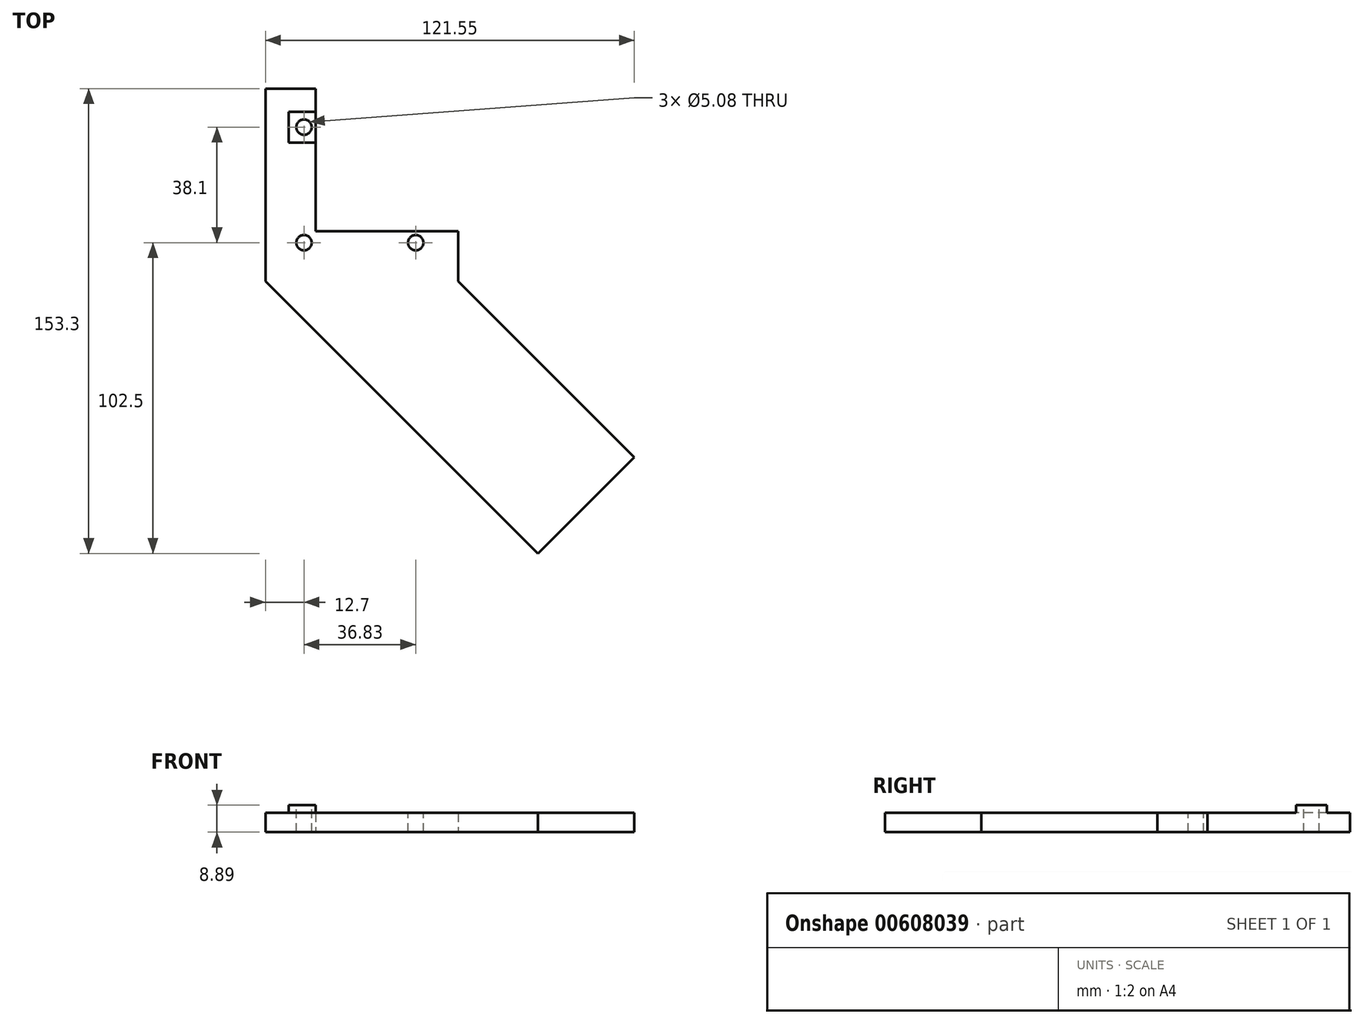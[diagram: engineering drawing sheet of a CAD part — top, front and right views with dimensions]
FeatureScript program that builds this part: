
annotation { "Feature Type Name" : "Feature", "Feature Type Description" : "" }
export const myFeature = defineFeature(function(context is Context, id is Id, definition is map)
    precondition{}
    {
        {
            var Q0;
            Q0=qCreatedBy(makeId("Top.planeOp"),FACE);
            var sketch = newSketch(context, id + "F0", { "sketchPlane" : qUnion([Q0])});
            skLineSegment(sketch, "E0", {"start": v(0, 0) * mm, "end": v(0, 63.5) * mm});
            skLineSegment(sketch, "E1", {"start": v(0, 63.5) * mm, "end": v(16.51, 63.5) * mm});
            skLineSegment(sketch, "E2", {"start": v(16.51, 63.5) * mm, "end": v(16.51, 16.5) * mm});
            skLineSegment(sketch, "E3", {"start": v(16.51, 16.5) * mm, "end": v(63.5, 16.51) * mm});
            skLineSegment(sketch, "E4", {"start": v(63.5, 16.51) * mm, "end": v(63.5, 0) * mm});
            skLineSegment(sketch, "E5", {"start": v(63.5, 0) * mm, "end": v(121.55, -58.05) * mm});
            skLineSegment(sketch, "E6", {"start": v(89.8, -89.8) * mm, "end": v(0, 0) * mm});
            skLineSegment(sketch, "E7", {"start": v(89.8, -89.8) * mm, "end": v(121.55, -58.05) * mm});
            skSolve(sketch);
        }
        {
            var Q0;
            Q0 = qSketchRegion(id + "F0", true);
            extrude(context, id + "F1", {"entities" : qUnion([Q0]), "depth" : 6.35 * mm, "offsetDistance" : 25.4 * mm});
        }
        {
            var Q0;
            Q0=makeQuery(id+"F1.opExtrude","CAP_FACE",FACE,{"disambiguationData":[OSD([sQuery(id+"F0.wireOp",EDGE,"E0"),sQuery(id+"F0.wireOp",EDGE,"E1"),sQuery(id+"F0.wireOp",EDGE,"E2"),sQuery(id+"F0.wireOp",EDGE,"E3"),sQuery(id+"F0.wireOp",EDGE,"E4"),sQuery(id+"F0.wireOp",EDGE,"E5"),sQuery(id+"F0.wireOp",EDGE,"BQdoBjQO-dgXR-ntd8-ExkX-L0m3NcibP9LL"),sQuery(id+"F0.wireOp",EDGE,"E6")])],"isStart":false});
            var sketch = newSketch(context, id + "F2", { "sketchPlane" : qUnion([Q0])});
            skCircle(sketch, "E8", {"center": v(12.7, 50.8) * mm, "radius": 2.54 * mm});
            skCircle(sketch, "E9", {"center": v(49.53, 12.7) * mm, "radius": 2.54 * mm});
            skCircle(sketch, "E10", {"center": v(12.7, 12.7) * mm, "radius": 2.54 * mm});
            skSolve(sketch);
        }
        {
            var Q0;
            Q0 = qSketchRegion(id + "F2", true);
            extrude(context, id + "F3", {"entities" : qUnion([Q0]), "operationType" : NewBodyOperationType.REMOVE, "oppositeDirection" : true, "depth" : 6.35 * mm, "offsetDistance" : 25.4 * mm});
        }
        {
            var Q0;
            Q0=makeQuery(id+"F1.opExtrude","CAP_FACE",FACE,{"disambiguationData":[OSD([sQuery(id+"F0.wireOp",EDGE,"E0"),sQuery(id+"F0.wireOp",EDGE,"E1"),sQuery(id+"F0.wireOp",EDGE,"E2"),sQuery(id+"F0.wireOp",EDGE,"E3"),sQuery(id+"F0.wireOp",EDGE,"E4"),sQuery(id+"F0.wireOp",EDGE,"E5"),sQuery(id+"F0.wireOp",EDGE,"E6"),sQuery(id+"F0.wireOp",EDGE,"E7")])],"isStart":false});
            var sketch = newSketch(context, id + "F4", { "sketchPlane" : qUnion([Q0])});
            skLineSegment(sketch, "E11.bottom", {"start": v(16.51, 55.88) * mm, "end": v(7.62, 55.88) * mm});
            skLineSegment(sketch, "E11.top", {"start": v(16.51, 45.72) * mm, "end": v(7.62, 45.72) * mm});
            skLineSegment(sketch, "E11.left", {"start": v(16.51, 55.88) * mm, "end": v(16.51, 45.72) * mm});
            skLineSegment(sketch, "E11.right", {"start": v(7.62, 55.88) * mm, "end": v(7.62, 45.72) * mm});
            skSolve(sketch);
        }
        {
            var Q0;
            Q0 = qSketchRegion(id + "F4", true);
            extrude(context, id + "F5", {"entities" : qUnion([Q0]), "operationType" : NewBodyOperationType.ADD, "depth" : 2.54 * mm, "offsetDistance" : 25.4 * mm});
        }
        {
            var Q0;
            Q0=makeQuery(id+"F5.opExtrude","CAP_FACE",FACE,{"disambiguationData":[OSD([sQuery(id+"F4.wireOp",EDGE,"E11.bottom"),sQuery(id+"F4.wireOp",EDGE,"E11.top"),sQuery(id+"F4.wireOp",EDGE,"E11.left"),sQuery(id+"F4.wireOp",EDGE,"E11.right")])],"isStart":false});
            var sketch = newSketch(context, id + "F6", { "sketchPlane" : qUnion([Q0])});
            skCircle(sketch, "E12", {"center": v(12.7, 50.8) * mm, "radius": 2.54 * mm});
            skSolve(sketch);
        }
        {
            var Q0;
            Q0 = qSketchRegion(id + "F6", true);
            extrude(context, id + "F7", {"entities" : qUnion([Q0]), "operationType" : NewBodyOperationType.REMOVE, "oppositeDirection" : true, "depth" : 25.4 * mm, "offsetDistance" : 25.4 * mm});
        }
    });
